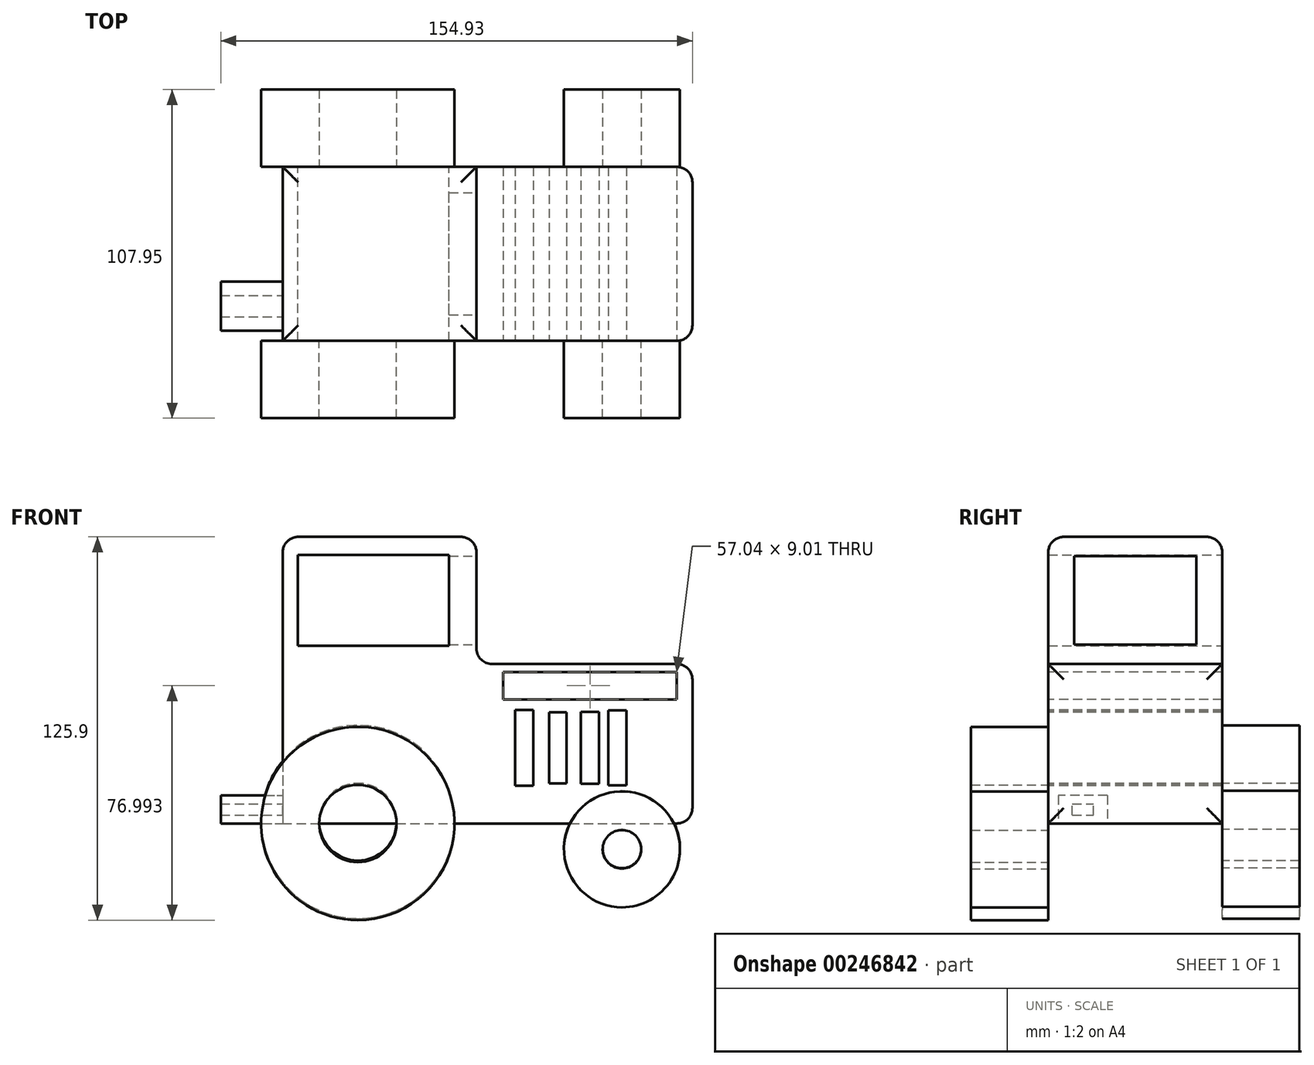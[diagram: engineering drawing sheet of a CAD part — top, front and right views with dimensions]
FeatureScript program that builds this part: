
annotation { "Feature Type Name" : "Feature", "Feature Type Description" : "" }
export const myFeature = defineFeature(function(context is Context, id is Id, definition is map)
    precondition{}
    {
        {
            var Q0;
            Q0=qCreatedBy(makeId("Front.planeOp"),FACE);
            var sketch = newSketch(context, id + "F0", { "sketchPlane" : qUnion([Q0])});
            skLineSegment(sketch, "E0.bottom", {"start": v(-63.66, 24.7) * mm, "end": v(70.95, 24.7) * mm});
            skLineSegment(sketch, "E0.top", {"start": v(-63.66, -27.68) * mm, "end": v(70.95, -27.68) * mm});
            skLineSegment(sketch, "E0.left", {"start": v(-63.66, 24.7) * mm, "end": v(-63.66, -27.68) * mm});
            skLineSegment(sketch, "E0.right", {"start": v(70.95, 24.7) * mm, "end": v(70.95, -27.68) * mm});
            skLineSegment(sketch, "E1.bottom", {"start": v(-63.64, 66.47) * mm, "end": v(0, 66.47) * mm});
            skLineSegment(sketch, "E1.top", {"start": v(-63.64, 24.7) * mm, "end": v(0, 24.7) * mm});
            skLineSegment(sketch, "E1.left", {"start": v(-63.64, 66.47) * mm, "end": v(-63.64, 24.7) * mm});
            skLineSegment(sketch, "E1.right", {"start": v(0, 66.47) * mm, "end": v(0, 24.7) * mm});
            skLineSegment(sketch, "E2.bottom", {"start": v(-8.95, 30.67) * mm, "end": v(-58.68, 30.67) * mm});
            skLineSegment(sketch, "E2.top", {"start": v(-8.95, 60.5) * mm, "end": v(-58.68, 60.5) * mm});
            skLineSegment(sketch, "E2.left", {"start": v(-8.95, 30.67) * mm, "end": v(-8.95, 60.5) * mm});
            skLineSegment(sketch, "E2.right", {"start": v(-58.68, 30.67) * mm, "end": v(-58.68, 60.5) * mm});
            skPoint(sketch, "E2.middle", {"position": v(-33.82, 45.59) * mm});
            skPoint(sketch, "E2.middle.positionSnap0", {"position": v(-63.64, 45.59) * mm});
            skPoint(sketch, "E2.centerSnap0", {"position": v(-63.64, 45.59) * mm});
            skSolve(sketch);
        }
        {
            var Q0;
            Q0=makeQuery(id+"F0.imprint","IMPRINT",FACE,{"disambiguationData":[TD([[makeQuery(id+"F0.imprint","IMPRINT",EDGE,{"derivedFrom":sQuery(id+"F0.wireOp",EDGE,"E0.top")}),1.0]])]});
            var Q1;
            Q1=makeQuery(id+"F0.imprint","IMPRINT",FACE,{"disambiguationData":[TD([[makeQuery(id+"F0.imprint","IMPRINT",EDGE,{"derivedFrom":sQuery(id+"F0.wireOp",EDGE,"E1.bottom")}),-1.0]])]});
            extrude(context, id + "F1", {"entities" : qUnion([Q0, Q1]), "depth" : 57.15 * mm});
        }
        {
            var Q0;
            Q0=qCreatedBy(makeId("Front.planeOp"),FACE);
            var sketch = newSketch(context, id + "F2", { "sketchPlane" : qUnion([Q0])});
            skCircle(sketch, "E3", {"center": v(47.81, -36.03) * mm, "radius": 19.05 * mm});
            skCircle(sketch, "E4", {"center": v(-38.95, -27.17) * mm, "radius": 31.75 * mm});
            skCircle(sketch, "E5", {"center": v(-38.95, -27.17) * mm, "radius": 12.7 * mm});
            skCircle(sketch, "E6", {"center": v(47.81, -36.03) * mm, "radius": 6.35 * mm});
            skSolve(sketch);
        }
        {
            var Q0;
            Q0 = qSketchRegion(id + "F2", true);
            extrude(context, id + "F3", {"entities" : qUnion([Q0]), "operationType" : NewBodyOperationType.ADD, "oppositeDirection" : true, "depth" : 25.4 * mm});
        }
        {
            var Q0;
            Q0=makeQuery(id+"F1.opExtrude","CAP_FACE",FACE,{"disambiguationData":[OSD([sQuery(id+"F0.wireOp",EDGE,"E0.bottom"),sQuery(id+"F0.wireOp",EDGE,"E0.top"),sQuery(id+"F0.wireOp",EDGE,"E0.left"),sQuery(id+"F0.wireOp",EDGE,"E0.right"),sQuery(id+"F0.wireOp",EDGE,"E1.bottom"),sQuery(id+"F0.wireOp",EDGE,"E1.left"),sQuery(id+"F0.wireOp",EDGE,"E1.right"),sQuery(id+"F0.wireOp",EDGE,"E2.bottom"),sQuery(id+"F0.wireOp",EDGE,"E2.top"),sQuery(id+"F0.wireOp",EDGE,"E2.left"),sQuery(id+"F0.wireOp",EDGE,"E2.right")])],"isStart":false});
            var sketch = newSketch(context, id + "F4", { "sketchPlane" : qUnion([Q0])});
            skCircle(sketch, "E7", {"center": v(-38.97, -27.68) * mm, "radius": 31.75 * mm});
            skCircle(sketch, "E8", {"center": v(47.8, -36.18) * mm, "radius": 19.05 * mm});
            skCircle(sketch, "E9", {"center": v(-38.97, -27.68) * mm, "radius": 12.7 * mm});
            skCircle(sketch, "E10", {"center": v(47.8, -36.18) * mm, "radius": 6.35 * mm});
            skSolve(sketch);
        }
        {
            var Q0;
            Q0 = qSketchRegion(id + "F4", true);
            extrude(context, id + "F5", {"entities" : qUnion([Q0]), "operationType" : NewBodyOperationType.ADD, "depth" : 25.4 * mm});
        }
        {
            var Q0;
            Q0=makeQuery(id+"F1.opExtrude","SWEPT_FACE",FACE,{"disambiguationData":[OSD([sQuery(id+"F0.wireOp",EDGE,"E1.right")])]});
            var sketch = newSketch(context, id + "F6", { "sketchPlane" : qUnion([Q0])});
            skLineSegment(sketch, "E11.bottom", {"start": v(-8.52, 31.07) * mm, "end": v(-48.63, 31.07) * mm});
            skLineSegment(sketch, "E11.top", {"start": v(-8.52, 60.1) * mm, "end": v(-48.63, 60.1) * mm});
            skLineSegment(sketch, "E11.left", {"start": v(-8.52, 31.07) * mm, "end": v(-8.52, 60.1) * mm});
            skLineSegment(sketch, "E11.right", {"start": v(-48.63, 31.07) * mm, "end": v(-48.63, 60.1) * mm});
            skPoint(sketch, "E11.middle", {"position": v(-28.58, 45.59) * mm});
            skPoint(sketch, "E11.middle.positionSnap0", {"position": v(0, 45.59) * mm});
            skPoint(sketch, "E11.middle.positionSnap1", {"position": v(-28.58, 66.47) * mm});
            skPoint(sketch, "E11.centerSnap0", {"position": v(0, 45.59) * mm});
            skPoint(sketch, "E11.centerSnap1", {"position": v(-28.58, 66.47) * mm});
            skSolve(sketch);
        }
        {
            var Q0;
            Q0=makeQuery(id+"F6.imprint","IMPRINT",FACE,{"disambiguationData":[TD([[makeQuery(id+"F6.imprint","IMPRINT",EDGE,{"derivedFrom":sQuery(id+"F6.wireOp",EDGE,"E11.bottom")}),-1.0]])]});
            extrude(context, id + "F7", {"entities" : qUnion([Q0]), "operationType" : NewBodyOperationType.REMOVE, "oppositeDirection" : true, "depth" : 25.4 * mm});
        }
        {
            var Q0;
            Q0=makeQuery(id+"F1.opExtrude","SWEPT_EDGE",EDGE,{"disambiguationData":[OSD([sQuery(id+"F0.wireOp",EDGE,"E0.bottom"),sQuery(id+"F0.wireOp",EDGE,"E1.top"),sQuery(id+"F0.wireOp",EDGE,"E1.right")])]});
            var Q1;
            Q1=makeQuery(id+"F1.opExtrude","SWEPT_EDGE",EDGE,{"disambiguationData":[OSD([sQuery(id+"F0.wireOp",EDGE,"E0.bottom"),sQuery(id+"F0.wireOp",EDGE,"E0.right")])]});
            var Q2;
            Q2=makeQuery(id+"F1.opExtrude","SWEPT_EDGE",EDGE,{"disambiguationData":[OSD([sQuery(id+"F0.wireOp",EDGE,"E0.top"),sQuery(id+"F0.wireOp",EDGE,"E0.right")])]});
            var Q3;
            Q3=makeQuery(id+"F1.opExtrude","CAP_EDGE",EDGE,{"disambiguationData":[OSD([sQuery(id+"F0.wireOp",EDGE,"E0.right")])],"isStart":true});
            var Q4;
            Q4=makeQuery(id+"F1.opExtrude","CAP_EDGE",EDGE,{"disambiguationData":[OSD([sQuery(id+"F0.wireOp",EDGE,"E0.right")])],"isStart":false});
            var Q5;
            Q5=makeQuery(id+"F1.opExtrude","CAP_EDGE",EDGE,{"disambiguationData":[OSD([sQuery(id+"F0.wireOp",EDGE,"E1.bottom")])],"isStart":false});
            var Q6;
            Q6=makeQuery(id+"F1.opExtrude","SWEPT_EDGE",EDGE,{"disambiguationData":[OSD([sQuery(id+"F0.wireOp",EDGE,"E1.bottom"),sQuery(id+"F0.wireOp",EDGE,"E1.right")])]});
            var Q7;
            Q7=makeQuery(id+"F1.opExtrude","CAP_EDGE",EDGE,{"disambiguationData":[OSD([sQuery(id+"F0.wireOp",EDGE,"E1.bottom")])],"isStart":true});
            var Q8;
            Q8=makeQuery(id+"F1.opExtrude","SWEPT_EDGE",EDGE,{"disambiguationData":[OSD([sQuery(id+"F0.wireOp",EDGE,"E1.bottom"),sQuery(id+"F0.wireOp",EDGE,"E1.left")])]});
            fillet(context, id + "F8", {"entities" : qUnion([Q0, Q1, Q2, Q3, Q4, Q5, Q6, Q7, Q8]), "radius" : 5.08 * mm, "tangentPropagation" : true, "allowEdgeOverflow" : false});
        }
        {
            var Q0;
            Q0=makeQuery(id+"F1.opExtrude","SWEPT_FACE",FACE,{"disambiguationData":[OSD([sQuery(id+"F0.wireOp",EDGE,"E0.left")])]});
            var sketch = newSketch(context, id + "F9", { "sketchPlane" : qUnion([Q0])});
            skLineSegment(sketch, "E12.bottom", {"start": v(37.7, -18.46) * mm, "end": v(53.8, -18.46) * mm});
            skLineSegment(sketch, "E12.top", {"start": v(37.7, -27.68) * mm, "end": v(53.8, -27.68) * mm});
            skLineSegment(sketch, "E12.left", {"start": v(37.7, -18.46) * mm, "end": v(37.7, -27.68) * mm});
            skLineSegment(sketch, "E12.right", {"start": v(53.8, -18.46) * mm, "end": v(53.8, -27.68) * mm});
            skLineSegment(sketch, "E13.bottom", {"start": v(49.28, -24.88) * mm, "end": v(42.23, -24.88) * mm});
            skLineSegment(sketch, "E13.top", {"start": v(49.28, -21.27) * mm, "end": v(42.23, -21.27) * mm});
            skLineSegment(sketch, "E13.left", {"start": v(49.28, -24.88) * mm, "end": v(49.28, -21.27) * mm});
            skLineSegment(sketch, "E13.right", {"start": v(42.23, -24.88) * mm, "end": v(42.23, -21.27) * mm});
            skPoint(sketch, "E13.middle", {"position": v(45.75, -23.07) * mm});
            skPoint(sketch, "E13.middle.positionSnap0", {"position": v(45.75, -27.68) * mm});
            skPoint(sketch, "E13.centerSnap0", {"position": v(45.75, -27.68) * mm});
            skSolve(sketch);
        }
        {
            var Q0;
            Q0 = qSketchRegion(id + "F9", true);
            extrude(context, id + "F10", {"entities" : qUnion([Q0]), "operationType" : NewBodyOperationType.ADD, "depth" : 20.32 * mm});
        }
        {
            var Q0;
            {var subQ14=sQuery(id+"F0.wireOp",EDGE,"E0.right");var subQ15=makeQuery(id+"F1.opExtrude","CAP_EDGE",EDGE,{"disambiguationData":[OSD([subQ14])],"isStart":false});Q0=makeQuery(id+"F4.imprint","IMPRINT",FACE,{"disambiguationData":[TD([[makeQuery(id+"F4.imprint","IMPRINT",EDGE,{"derivedFrom":subQ15}),-1.0]])]});}
            var sketch = newSketch(context, id + "F11", { "sketchPlane" : qUnion([Q0])});
            skLineSegment(sketch, "E14.bottom", {"start": v(65.8, 13.06) * mm, "end": v(8.76, 13.06) * mm});
            skLineSegment(sketch, "E14.top", {"start": v(65.8, 22.07) * mm, "end": v(8.76, 22.07) * mm});
            skLineSegment(sketch, "E14.left", {"start": v(65.8, 13.06) * mm, "end": v(65.8, 22.07) * mm});
            skLineSegment(sketch, "E14.right", {"start": v(8.76, 13.06) * mm, "end": v(8.76, 22.07) * mm});
            skPoint(sketch, "E14.middle", {"position": v(37.29, 17.56) * mm});
            skLineSegment(sketch, "E15.bottom", {"start": v(18.67, -15.31) * mm, "end": v(12.67, -15.31) * mm});
            skLineSegment(sketch, "E15.top", {"start": v(18.67, 9.6) * mm, "end": v(12.67, 9.6) * mm});
            skLineSegment(sketch, "E15.left", {"start": v(18.67, -15.31) * mm, "end": v(18.67, 9.6) * mm});
            skLineSegment(sketch, "E15.right", {"start": v(12.67, -15.31) * mm, "end": v(12.67, 9.6) * mm});
            skPoint(sketch, "E15.middle", {"position": v(15.67, -2.85) * mm});
            skLineSegment(sketch, "E16.bottom", {"start": v(29.63, -14.56) * mm, "end": v(23.93, -14.56) * mm});
            skLineSegment(sketch, "E16.top", {"start": v(29.63, 8.86) * mm, "end": v(23.93, 8.86) * mm});
            skLineSegment(sketch, "E16.left", {"start": v(29.63, -14.56) * mm, "end": v(29.63, 8.86) * mm});
            skLineSegment(sketch, "E16.right", {"start": v(23.93, -14.56) * mm, "end": v(23.93, 8.86) * mm});
            skPoint(sketch, "E16.middle", {"position": v(26.78, -2.85) * mm});
            skLineSegment(sketch, "E17.bottom", {"start": v(49.3, -15.16) * mm, "end": v(43.3, -15.16) * mm});
            skLineSegment(sketch, "E17.top", {"start": v(49.3, 9.46) * mm, "end": v(43.3, 9.46) * mm});
            skLineSegment(sketch, "E17.left", {"start": v(49.3, -15.16) * mm, "end": v(49.3, 9.46) * mm});
            skLineSegment(sketch, "E17.right", {"start": v(43.3, -15.16) * mm, "end": v(43.3, 9.46) * mm});
            skPoint(sketch, "E17.middle", {"position": v(46.3, -2.85) * mm});
            skLineSegment(sketch, "E18.bottom", {"start": v(40.29, -14.71) * mm, "end": v(34.28, -14.71) * mm});
            skLineSegment(sketch, "E18.top", {"start": v(40.29, 9) * mm, "end": v(34.28, 9) * mm});
            skLineSegment(sketch, "E18.left", {"start": v(40.29, -14.71) * mm, "end": v(40.29, 9) * mm});
            skLineSegment(sketch, "E18.right", {"start": v(34.28, -14.71) * mm, "end": v(34.28, 9) * mm});
            skPoint(sketch, "E18.middle", {"position": v(37.29, -2.85) * mm});
            skSolve(sketch);
        }
        {
            var Q0;
            Q0 = qSketchRegion(id + "F11", true);
            extrude(context, id + "F12", {"entities" : qUnion([Q0]), "operationType" : NewBodyOperationType.REMOVE, "oppositeDirection" : true, "depth" : 63.25 * mm});
        }
    });
